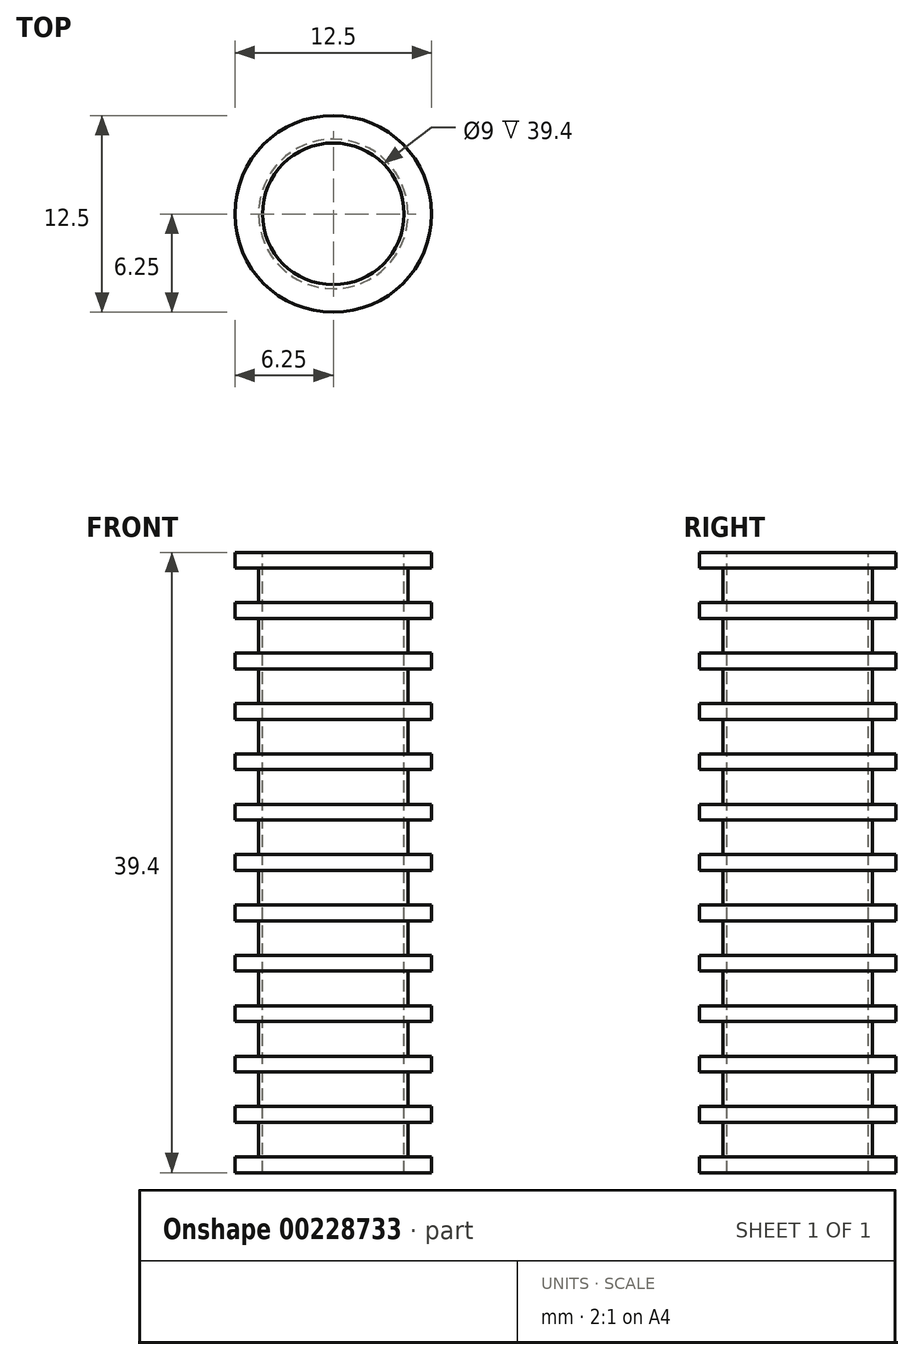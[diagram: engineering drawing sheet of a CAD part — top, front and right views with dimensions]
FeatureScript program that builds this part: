
annotation { "Feature Type Name" : "Feature", "Feature Type Description" : "" }
export const myFeature = defineFeature(function(context is Context, id is Id, definition is map)
    precondition{}
    {
        {
            var Q0;
            Q0=qCreatedBy(makeId("Front.planeOp"),FACE);
            var sketch = newSketch(context, id + "F0", { "sketchPlane" : qUnion([Q0])});
            skLineSegment(sketch, "E0", {"start": v(6.25, 0) * mm, "end": v(6.25, 1) * mm});
            skLineSegment(sketch, "E1", {"start": v(6.25, 1) * mm, "end": v(4.75, 1) * mm});
            skLineSegment(sketch, "E2", {"start": v(4.75, 1) * mm, "end": v(4.75, 3.2) * mm});
            skLineSegment(sketch, "E3", {"start": v(4.75, 3.2) * mm, "end": v(6.25, 3.2) * mm});
            skLineSegment(sketch, "E4", {"start": v(6.25, 3.2) * mm, "end": v(6.25, 4.2) * mm});
            skLineSegment(sketch, "E5", {"start": v(6.25, 4.2) * mm, "end": v(4.75, 4.2) * mm});
            skLineSegment(sketch, "E6", {"start": v(4.75, 4.2) * mm, "end": v(4.75, 6.4) * mm});
            skLineSegment(sketch, "E7", {"start": v(4.75, 6.4) * mm, "end": v(6.25, 6.4) * mm});
            skLineSegment(sketch, "E8", {"start": v(6.25, 6.4) * mm, "end": v(6.25, 7.4) * mm});
            skLineSegment(sketch, "E9", {"start": v(6.25, 7.4) * mm, "end": v(4.75, 7.4) * mm});
            skLineSegment(sketch, "E10", {"start": v(4.75, 7.4) * mm, "end": v(4.75, 9.6) * mm});
            skLineSegment(sketch, "E11", {"start": v(4.75, 9.6) * mm, "end": v(6.25, 9.6) * mm});
            skLineSegment(sketch, "E12", {"start": v(6.25, 9.6) * mm, "end": v(6.25, 10.6) * mm});
            skLineSegment(sketch, "E13", {"start": v(6.25, 10.6) * mm, "end": v(4.75, 10.6) * mm});
            skLineSegment(sketch, "E14", {"start": v(4.75, 10.6) * mm, "end": v(4.75, 12.8) * mm});
            skLineSegment(sketch, "E15", {"start": v(4.75, 12.8) * mm, "end": v(6.25, 12.8) * mm});
            skLineSegment(sketch, "E16", {"start": v(6.25, 12.8) * mm, "end": v(6.25, 13.8) * mm});
            skLineSegment(sketch, "E17", {"start": v(6.25, 13.8) * mm, "end": v(4.75, 13.8) * mm});
            skLineSegment(sketch, "E18", {"start": v(4.75, 13.8) * mm, "end": v(4.75, 16) * mm});
            skLineSegment(sketch, "E19", {"start": v(4.75, 16) * mm, "end": v(6.25, 16) * mm});
            skLineSegment(sketch, "E20", {"start": v(6.25, 16) * mm, "end": v(6.25, 17) * mm});
            skLineSegment(sketch, "E21", {"start": v(6.25, 17) * mm, "end": v(4.75, 17) * mm});
            skLineSegment(sketch, "E22", {"start": v(4.75, 17) * mm, "end": v(4.75, 19.2) * mm});
            skLineSegment(sketch, "E23", {"start": v(4.75, 19.2) * mm, "end": v(6.25, 19.2) * mm});
            skLineSegment(sketch, "E24", {"start": v(6.25, 19.2) * mm, "end": v(6.25, 20.2) * mm});
            skLineSegment(sketch, "E25", {"start": v(6.25, 20.2) * mm, "end": v(4.75, 20.2) * mm});
            skLineSegment(sketch, "E26", {"start": v(4.75, 20.2) * mm, "end": v(4.75, 22.4) * mm});
            skLineSegment(sketch, "E27", {"start": v(4.75, 22.4) * mm, "end": v(6.25, 22.4) * mm});
            skLineSegment(sketch, "E28", {"start": v(6.25, 22.4) * mm, "end": v(6.25, 23.4) * mm});
            skLineSegment(sketch, "E29", {"start": v(6.25, 23.4) * mm, "end": v(4.75, 23.4) * mm});
            skLineSegment(sketch, "E30", {"start": v(4.75, 23.4) * mm, "end": v(4.75, 25.6) * mm});
            skLineSegment(sketch, "E31", {"start": v(4.75, 25.6) * mm, "end": v(6.25, 25.6) * mm});
            skLineSegment(sketch, "E32", {"start": v(6.25, 25.6) * mm, "end": v(6.25, 26.6) * mm});
            skLineSegment(sketch, "E33", {"start": v(6.25, 26.6) * mm, "end": v(4.75, 26.6) * mm});
            skLineSegment(sketch, "E34", {"start": v(4.75, 26.6) * mm, "end": v(4.75, 28.8) * mm});
            skLineSegment(sketch, "E35", {"start": v(4.75, 28.8) * mm, "end": v(6.25, 28.8) * mm});
            skLineSegment(sketch, "E36", {"start": v(6.25, 28.8) * mm, "end": v(6.25, 29.8) * mm});
            skLineSegment(sketch, "E37", {"start": v(6.25, 29.8) * mm, "end": v(4.75, 29.8) * mm});
            skLineSegment(sketch, "E38", {"start": v(4.75, 29.8) * mm, "end": v(4.75, 32) * mm});
            skLineSegment(sketch, "E39", {"start": v(4.75, 32) * mm, "end": v(6.25, 32) * mm});
            skLineSegment(sketch, "E40", {"start": v(6.25, 32) * mm, "end": v(6.25, 33) * mm});
            skLineSegment(sketch, "E41", {"start": v(6.25, 33) * mm, "end": v(4.75, 33) * mm});
            skLineSegment(sketch, "E42", {"start": v(4.75, 33) * mm, "end": v(4.75, 35.2) * mm});
            skLineSegment(sketch, "E43", {"start": v(4.75, 35.2) * mm, "end": v(6.25, 35.2) * mm});
            skLineSegment(sketch, "E44", {"start": v(6.25, 35.2) * mm, "end": v(6.25, 36.2) * mm});
            skLineSegment(sketch, "E45", {"start": v(6.25, 36.2) * mm, "end": v(4.75, 36.2) * mm});
            skLineSegment(sketch, "E46", {"start": v(4.75, 36.2) * mm, "end": v(4.75, 38.4) * mm});
            skLineSegment(sketch, "E47", {"start": v(4.75, 38.4) * mm, "end": v(6.25, 38.4) * mm});
            skLineSegment(sketch, "E48", {"start": v(6.25, 39.4) * mm, "end": v(4.75, 39.4) * mm});
            skLineSegment(sketch, "E49", {"start": v(4.75, 39.4) * mm, "end": v(0, 39.4) * mm});
            skLineSegment(sketch, "E50", {"start": v(6.25, 39.4) * mm, "end": v(6.25, 38.4) * mm});
            skLineSegment(sketch, "E51", {"start": v(0, 39.4) * mm, "end": v(0, 0) * mm});
            skLineSegment(sketch, "E52", {"start": v(0, 0) * mm, "end": v(6.25, 0) * mm});
            skSolve(sketch);
        }
        {
            var Q0;
            Q0=makeQuery(id+"F0.imprint","IMPRINT",FACE,{"disambiguationData":[TD([[makeQuery(id+"F0.imprint","IMPRINT",EDGE,{"derivedFrom":sQuery(id+"F0.wireOp",EDGE,"E0")}),1.0]])]});
            var Q1;
            Q1=sQuery(id+"F0.wireOp",EDGE,"E51");
            revolve(context, id + "F1", {"entities" : qUnion([Q0]), "axis" : qUnion([Q1]), "revolveType" : RevolveType.FULL});
        }
        {
            var Q0;
            Q0=makeQuery(id+"F1.opRevolve","SWEPT_FACE",FACE,{"disambiguationData":[OSD([sQuery(id+"F0.wireOp",EDGE,"E48"),sQuery(id+"F0.wireOp",EDGE,"E49")])]});
            var sketch = newSketch(context, id + "F2", { "sketchPlane" : qUnion([Q0])});
            skCircle(sketch, "E53", {"center": v(0, 0) * mm, "radius": 4.5 * mm});
            skSolve(sketch);
        }
        {
            var Q0;
            Q0=makeQuery(id+"F2.imprint","IMPRINT",FACE,{"disambiguationData":[TD([[makeQuery(id+"F2.imprint","IMPRINT",EDGE,{"derivedFrom":sQuery(id+"F2.wireOp",EDGE,"E53")}),1.0]])]});
            var Q1;
            Q1=makeQuery(id+"F1.opRevolve","SWEPT_FACE",FACE,{"disambiguationData":[OSD([sQuery(id+"F0.wireOp",EDGE,"E52")])]});
            extrude(context, id + "F3", {"entities" : qUnion([Q0]), "operationType" : NewBodyOperationType.REMOVE, "endBound" : BoundingType.UP_TO_SURFACE, "oppositeDirection" : true, "endBoundEntityFace" : qUnion([Q1]), "depth" : 25 * mm});
        }
    });
